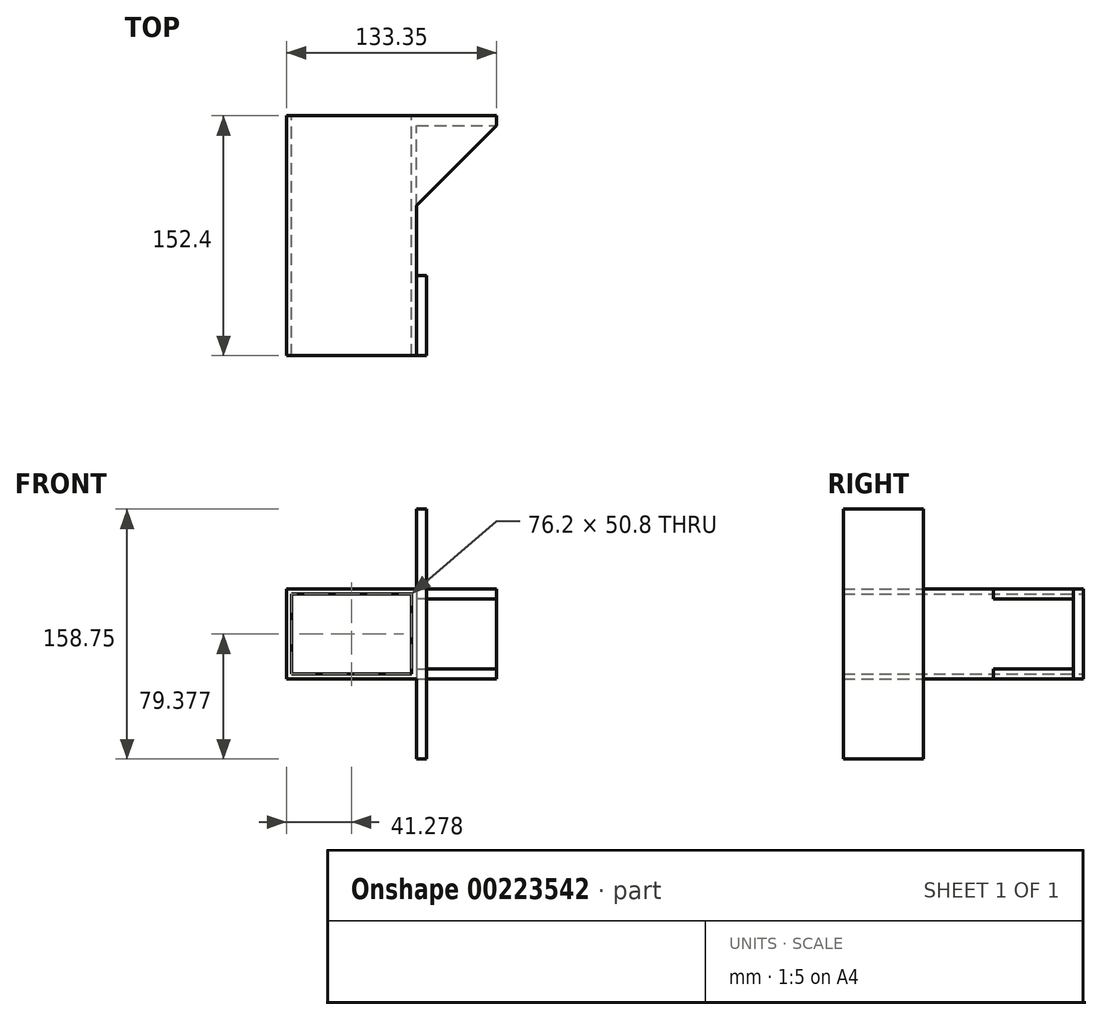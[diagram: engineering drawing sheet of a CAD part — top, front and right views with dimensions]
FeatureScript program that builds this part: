
annotation { "Feature Type Name" : "Feature", "Feature Type Description" : "" }
export const myFeature = defineFeature(function(context is Context, id is Id, definition is map)
    precondition{}
    {
        {
            var Q0;
            Q0=qCreatedBy(makeId("Front.planeOp"),FACE);
            var sketch = newSketch(context, id + "F0", { "sketchPlane" : qUnion([Q0])});
            skLineSegment(sketch, "E0.bottom", {"start": v(-34.37, 6.03) * mm, "end": v(41.83, 6.03) * mm});
            skLineSegment(sketch, "E0.top", {"start": v(-34.37, -44.77) * mm, "end": v(41.83, -44.77) * mm});
            skLineSegment(sketch, "E0.left", {"start": v(-34.37, 6.03) * mm, "end": v(-34.37, -44.77) * mm});
            skLineSegment(sketch, "E0.right", {"start": v(41.83, 6.03) * mm, "end": v(41.83, -44.77) * mm});
            skLineSegment(sketch, "E1.0", {"start": v(-37.55, 9.2) * mm, "end": v(45, 9.2) * mm});
            skLineSegment(sketch, "E1.1", {"start": v(-37.55, 9.2) * mm, "end": v(-37.55, -47.95) * mm});
            skLineSegment(sketch, "E1.2", {"start": v(-37.55, -47.95) * mm, "end": v(45, -47.95) * mm});
            skLineSegment(sketch, "E1.3", {"start": v(45, 9.2) * mm, "end": v(45, -47.95) * mm});
            skSolve(sketch);
        }
        {
            var Q0;
            Q0=makeQuery(id+"F0.imprint","IMPRINT",FACE,{"disambiguationData":[TD([[makeQuery(id+"F0.imprint","IMPRINT",EDGE,{"derivedFrom":sQuery(id+"F0.wireOp",EDGE,"E0.bottom")}),1.0]])]});
            extrude(context, id + "F1", {"entities" : qUnion([Q0]), "depth" : 152.4 * mm});
        }
        {
            var Q0;
            Q0=makeQuery(id+"F1.opExtrude","SWEPT_FACE",FACE,{"disambiguationData":[OSD([sQuery(id+"F0.wireOp",EDGE,"E1.3")])]});
            var sketch = newSketch(context, id + "F2", { "sketchPlane" : qUnion([Q0])});
            skLineSegment(sketch, "E2.bottom", {"start": v(0, 9.2) * mm, "end": v(-6.35, 9.2) * mm});
            skLineSegment(sketch, "E2.top", {"start": v(0, -47.95) * mm, "end": v(-6.35, -47.95) * mm});
            skLineSegment(sketch, "E2.left", {"start": v(0, 9.2) * mm, "end": v(0, -47.95) * mm});
            skLineSegment(sketch, "E2.right", {"start": v(-6.35, 9.2) * mm, "end": v(-6.35, -47.95) * mm});
            skSolve(sketch);
        }
        {
            var Q0;
            Q0=qSketchRegion(id+"F2",true);
            extrude(context, id + "F3", {"entities" : qUnion([Q0]), "operationType" : NewBodyOperationType.ADD, "depth" : 50.8 * mm});
        }
        {
            var Q0;
            Q0=makeQuery(id+"F3.opExtrude","SWEPT_FACE",FACE,{"disambiguationData":[OSD([sQuery(id+"F2.wireOp",EDGE,"E2.right")])]});
            var sketch = newSketch(context, id + "F4", { "sketchPlane" : qUnion([Q0])});
            skLineSegment(sketch, "E3.bottom", {"start": v(45, -47.95) * mm, "end": v(95.8, -47.95) * mm});
            skLineSegment(sketch, "E3.top", {"start": v(45, -41.6) * mm, "end": v(95.8, -41.6) * mm});
            skLineSegment(sketch, "E3.left", {"start": v(45, -47.95) * mm, "end": v(45, -41.6) * mm});
            skLineSegment(sketch, "E3.right", {"start": v(95.8, -47.95) * mm, "end": v(95.8, -41.6) * mm});
            skLineSegment(sketch, "E4.bottom", {"start": v(95.8, 9.2) * mm, "end": v(45, 9.2) * mm});
            skLineSegment(sketch, "E4.top", {"start": v(95.8, 2.85) * mm, "end": v(45, 2.85) * mm});
            skLineSegment(sketch, "E4.left", {"start": v(95.8, 9.2) * mm, "end": v(95.8, 2.85) * mm});
            skLineSegment(sketch, "E4.right", {"start": v(45, 9.2) * mm, "end": v(45, 2.85) * mm});
            skSolve(sketch);
        }
        {
            var Q0;
            Q0=qSketchRegion(id+"F4",true);
            extrude(context, id + "F5", {"entities" : qUnion([Q0]), "operationType" : NewBodyOperationType.ADD, "depth" : 50.8 * mm});
        }
        {
            var Q0;
            Q0=makeQuery(id+"F5.boolean.opBoolean","MERGE",FACE,{"derivedFrom":[makeQuery(id+"F3.boolean.opBoolean","MERGE",FACE,{"derivedFrom":[makeQuery(id+"F1.opExtrude","SWEPT_FACE",FACE,{"disambiguationData":[OSD([sQuery(id+"F0.wireOp",EDGE,"E1.0")])]}),makeQuery(id+"F3.opExtrude","SWEPT_FACE",FACE,{"disambiguationData":[OSD([sQuery(id+"F2.wireOp",EDGE,"E2.bottom")])]})]}),makeQuery(id+"F5.opExtrude","SWEPT_FACE",FACE,{"disambiguationData":[OSD([sQuery(id+"F4.wireOp",EDGE,"E4.bottom")])]})]});
            var sketch = newSketch(context, id + "F6", { "sketchPlane" : qUnion([Q0])});
            skLineSegment(sketch, "E5", {"start": v(45, -57.15) * mm, "end": v(95.8, -6.35) * mm});
            skLineSegment(sketch, "E6", {"start": v(45, -57.15) * mm, "end": v(95.8, -57.15) * mm});
            skLineSegment(sketch, "E7", {"start": v(95.8, -57.15) * mm, "end": v(95.8, -6.35) * mm});
            skSolve(sketch);
        }
        {
            var Q0;
            Q0=qSketchRegion(id+"F6",true);
            extrude(context, id + "F7", {"entities" : qUnion([Q0]), "operationType" : NewBodyOperationType.REMOVE, "oppositeDirection" : true, "depth" : 118.62 * mm});
        }
        {
            var Q0;
            Q0=makeQuery(id+"F1.opExtrude","SWEPT_FACE",FACE,{"disambiguationData":[OSD([sQuery(id+"F0.wireOp",EDGE,"E1.3")])]});
            var sketch = newSketch(context, id + "F8", { "sketchPlane" : qUnion([Q0])});
            skLineSegment(sketch, "E8.bottom", {"start": v(-152.4, 60) * mm, "end": v(-101.6, 60) * mm});
            skLineSegment(sketch, "E8.top", {"start": v(-152.4, -98.75) * mm, "end": v(-101.6, -98.75) * mm});
            skLineSegment(sketch, "E8.left", {"start": v(-152.4, 60) * mm, "end": v(-152.4, -98.75) * mm});
            skLineSegment(sketch, "E8.right", {"start": v(-101.6, 60) * mm, "end": v(-101.6, -98.75) * mm});
            skSolve(sketch);
        }
        {
            var Q0;
            Q0=qSketchRegion(id+"F8",true);
            extrude(context, id + "F9", {"entities" : qUnion([Q0]), "operationType" : NewBodyOperationType.ADD, "depth" : 6.35 * mm});
        }
    });
